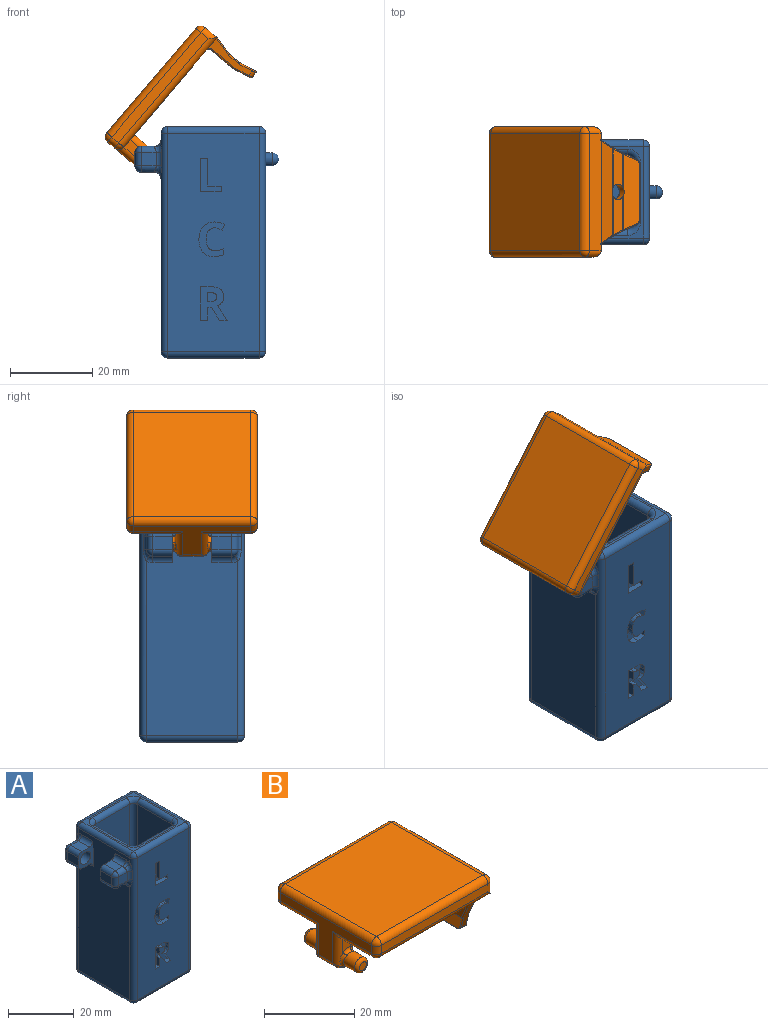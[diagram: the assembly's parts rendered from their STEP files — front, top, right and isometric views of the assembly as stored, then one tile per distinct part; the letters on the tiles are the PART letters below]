
ASSEMBLY  parts=2 mates=1
PART A: 139 faces, bbox 34.9x25.4x56.2 mm
  f0: plane 53.02x22.23mm, normal (-1,0,0), area 1058.3mm2, adj f78,f79,f88,f89,f97,f102,f119,f120
  f1: plane 22.23x22.23mm, normal (0,0,1), area 63.5mm2, adj f60,f65,f66,f69,f70,f72,f73,f74
  f2: plane 53.02x22.23mm, normal (0,-1,0), area 1099mm2, adj f17,f18,f19,f20,f21,f22,f23,f24
  f3: plane 53.02x22.23mm, normal (1,0,0), area 1170.5mm2, adj f81,f82,f90,f91,f137
  f4: plane 53.02x22.23mm, normal (0,1,0), area 1178.4mm2, adj f80,f89,f90,f94
  f5: plane 22.23x22.23mm, normal (0,0,-1), area 494mm2, adj f75,f79,f80,f81
  f6: plane 49.21x14.61mm, normal (1,0,0), area 718.7mm2, adj f58,f59,f68,f69
  f7: plane 49.21x14.61mm, normal (0,-1,0), area 718.7mm2, adj f63,f68,f71,f74
  f8: plane 49.21x14.61mm, normal (-1,0,0), area 718.7mm2, adj f61,f62,f70,f71
  f9: plane 49.21x14.61mm, normal (0,1,0), area 718.7mm2, adj f55,f59,f60,f61
  f10: plane 14.61x14.61mm, normal (0,0,1), area 213.3mm2, adj f55,f58,f62,f63
  f11: plane 2.21x1.59mm, normal (-1,0,0), area 3.5mm2, adj f12,f29,f30,f54
  f12: plane 1.59x0.53mm, normal (0,0,1), area 0.8mm2, adj f11,f13,f30,f54
  f13: extruded ~1.59x1.24mm, area 2mm2, adj f12,f14,f30,f54
  f14: extruded ~1.59x0.83mm, area 1.5mm2, adj f13,f15,f30,f54
  f15: extruded ~1.59x0.86mm, area 1.6mm2, adj f14,f16,f30,f54
  f16: extruded ~1.59x1.22mm, area 2mm2, adj f15,f29,f30,f54
  f17: plane 1.59x0.92mm, normal (0,0,1), area 1.5mm2, adj f2,f18,f28,f30
  f18: plane 3.14x1.95mm, normal (0.85,0,0.53), area 5.9mm2, adj f2,f17,f19,f30
  f19: plane 1.93x1.59mm, normal (0,0,1), area 3.1mm2, adj f2,f18,f20,f30
  f20: plane 3.57x2.41mm, normal (-0.83,0,-0.56), area 6.8mm2, adj f2,f19,f21,f30
  f21: extruded ~1.59x1.13mm, area 2.3mm2, adj f2,f20,f22,f30
  f22: extruded ~1.59x1.28mm, area 2.2mm2, adj f2,f21,f23,f30
  f23: extruded ~1.85x1.59mm, area 3.3mm2, adj f2,f22,f24,f30
  f24: extruded ~2.47x1.59mm, area 4.1mm2, adj f2,f23,f25,f30
  f25: plane 2.38x1.59mm, normal (0,0,-1), area 3.8mm2, adj f2,f24,f26,f30
  f26: plane 8.19x1.59mm, normal (1,0,0), area 13mm2, adj f2,f25,f27,f30
  f27: plane 1.74x1.59mm, normal (0,0,1), area 2.8mm2, adj f2,f26,f28,f30
  f28: plane 3.14x1.59mm, normal (-1,0,0), area 5mm2, adj f2,f17,f27,f30
  f29: plane 1.59x0.56mm, normal (0,0,-1), area 0.9mm2, adj f11,f16,f30,f54
  f30: plane 8.19x6.54mm, normal (0,-1,0), area 32.7mm2, adj f11,f12,f13,f14,f15,f16,f17,f18
  f31: extruded ~1.59x0.91mm, area 1.5mm2, adj f2,f32,f45,f46
  f32: extruded ~1.59x0.92mm, area 1.6mm2, adj f2,f31,f33,f46
  f33: plane 1.59x1.41mm, normal (-0.93,0,0.37), area 2.4mm2, adj f2,f32,f34,f46
  f34: extruded ~2.4x1.59mm, area 3.9mm2, adj f2,f33,f35,f46
  f35: extruded ~2.04x1.59mm, area 3.4mm2, adj f2,f34,f36,f46
  f36: extruded ~1.59x1.47mm, area 3.2mm2, adj f2,f35,f37,f46
  f37: extruded ~2.24x1.59mm, area 3.7mm2, adj f2,f36,f38,f46
  f38: extruded ~3.11x1.59mm, area 5.3mm2, adj f2,f37,f39,f46
  f39: extruded ~2.73x1.59mm, area 4.8mm2, adj f2,f38,f40,f46
  f40: extruded ~2.25x1.59mm, area 3.7mm2, adj f2,f39,f41,f46
  f41: plane 1.59x1.45mm, normal (-1,0,0), area 2.3mm2, adj f2,f40,f42,f46
  f42: extruded ~2.09x1.59mm, area 3.4mm2, adj f2,f41,f43,f46
  f43: extruded ~2.74x2.05mm, area 6.2mm2, adj f2,f42,f44,f46
  f44: extruded ~2.05x1.59mm, area 3.4mm2, adj f2,f43,f45,f46
  f45: extruded ~1.59x1.52mm, area 2.8mm2, adj f2,f31,f44,f46
  f46: plane 8.41x6.24mm, normal (0,-1,0), area 23.5mm2, adj f31,f32,f33,f34,f35,f36,f37,f38
  f47: plane 5.06x1.59mm, normal (0,0,1), area 8mm2, adj f2,f48,f52,f53
  f48: plane 1.59x1.43mm, normal (-1,0,0), area 2.3mm2, adj f2,f47,f49,f53
  f49: plane 3.32x1.59mm, normal (0,0,-1), area 5.3mm2, adj f2,f48,f50,f53
  f50: plane 6.75x1.59mm, normal (-1,0,0), area 10.7mm2, adj f2,f49,f51,f53
  f51: plane 1.74x1.59mm, normal (0,0,-1), area 2.8mm2, adj f2,f50,f52,f53
  f52: plane 8.19x1.59mm, normal (1,0,0), area 13mm2, adj f2,f47,f51,f53
  f53: plane 8.19x5.06mm, normal (0,-1,0), area 19mm2, adj f47,f48,f49,f50,f51,f52
  f54: plane 2.21x2.17mm, normal (0,-1,0), area 4.2mm2, adj f11,f12,f13,f14,f15,f16,f29
  f55: cylinder r=1.59mm len=14.61mm, axis (-1,0,0), area 36.4mm2, adj f9,f10,f56,f57
  f56: sphere r=1.59mm, area 4mm2, adj f55,f58,f59
  f57: sphere r=1.59mm, area 4mm2, adj f55,f61,f62
  f58: cylinder r=1.59mm len=14.61mm, axis (0,1,0), area 36.4mm2, adj f6,f10,f56,f64
  f59: cylinder r=1.59mm len=49.21mm, axis (0,0,-1), area 122.7mm2, adj f6,f9,f56,f65
  f60: cylinder r=1.59mm len=14.61mm, axis (1,0,0), area 36.4mm2, adj f1,f9,f65,f66
  f61: cylinder r=1.59mm len=49.21mm, axis (0,0,1), area 122.7mm2, adj f8,f9,f57,f66
  f62: cylinder r=1.59mm len=14.61mm, axis (0,-1,0), area 36.4mm2, adj f8,f10,f57,f67
  f63: cylinder r=1.59mm len=14.61mm, axis (1,0,0), area 36.4mm2, adj f7,f10,f64,f67
  f64: sphere r=1.59mm, area 4mm2, adj f58,f63,f68
  f65: torus R=3.17mm, axis (0,0,1), area 8.5mm2, adj f1,f59,f60,f69
  f66: torus R=3.17mm, axis (0,0,1), area 8.5mm2, adj f1,f60,f61,f70
  f67: sphere r=1.59mm, area 4mm2, adj f62,f63,f71
  f68: cylinder r=1.59mm len=49.21mm, axis (0,0,1), area 122.7mm2, adj f6,f7,f64,f72
  f69: cylinder r=1.59mm len=14.61mm, axis (0,-1,0), area 36.4mm2, adj f1,f6,f65,f72
  f70: cylinder r=1.59mm len=14.61mm, axis (0,1,0), area 36.4mm2, adj f1,f8,f66,f73
  f71: cylinder r=1.59mm len=49.21mm, axis (0,0,-1), area 122.7mm2, adj f7,f8,f67,f73
  f72: torus R=3.17mm, axis (0,0,1), area 8.5mm2, adj f1,f68,f69,f74
  f73: torus R=3.17mm, axis (0,0,1), area 8.5mm2, adj f1,f70,f71,f74
  f74: cylinder r=1.59mm len=14.61mm, axis (-1,0,0), area 36.4mm2, adj f1,f7,f72,f73
  f75: cylinder r=1.59mm len=22.23mm, axis (1,0,0), area 55.4mm2, adj f2,f5,f76,f77
  f76: sphere r=1.59mm, area 4mm2, adj f75,f78,f79
  f77: sphere r=1.59mm, area 4mm2, adj f75,f81,f82
  f78: cylinder r=1.59mm len=53.02mm, axis (0,0,1), area 126.4mm2, adj f0,f2,f76,f84,f128,f129,f130
  f79: cylinder r=1.59mm len=22.23mm, axis (0,-1,0), area 55.4mm2, adj f0,f5,f76,f85
  f80: cylinder r=1.59mm len=22.23mm, axis (-1,0,0), area 55.4mm2, adj f4,f5,f85,f86
  f81: cylinder r=1.59mm len=22.23mm, axis (0,1,0), area 55.4mm2, adj f3,f5,f77,f86
  f82: cylinder r=1.59mm len=53.02mm, axis (0,0,-1), area 132.2mm2, adj f2,f3,f77,f87
  f83: cylinder r=1.59mm len=22.23mm, axis (-1,0,0), area 55.4mm2, adj f1,f2,f84,f87
  f84: sphere r=1.59mm, area 4mm2, adj f78,f83,f88
  f85: sphere r=1.59mm, area 4mm2, adj f79,f80,f89
  f86: sphere r=1.59mm, area 4mm2, adj f80,f81,f90
  f87: sphere r=1.59mm, area 4mm2, adj f82,f83,f91
  f88: cylinder r=1.59mm len=22.23mm, axis (0,1,0), area 55.4mm2, adj f0,f1,f84,f92
  f89: cylinder r=1.59mm len=53.02mm, axis (0,0,-1), area 126.4mm2, adj f0,f4,f85,f92,f121,f122,f123
  f90: cylinder r=1.59mm len=53.02mm, axis (0,0,1), area 132.2mm2, adj f3,f4,f86,f93
  f91: cylinder r=1.59mm len=22.23mm, axis (0,-1,0), area 55.4mm2, adj f1,f3,f87,f93
  f92: sphere r=1.59mm, area 4mm2, adj f88,f89,f94
  f93: sphere r=1.59mm, area 4mm2, adj f90,f91,f94
  f94: cylinder r=1.59mm len=22.23mm, axis (1,0,0), area 55.4mm2, adj f1,f4,f92,f93
  f95: plane 3.6x3.18mm, normal (0,1,0), area 11.4mm2, adj f113,f116,f118,f122
  f96: plane 4.76x3.18mm, normal (0,0,-1), area 15.1mm2, adj f97,f112,f113,f125
  f97: plane 9.53x6.35mm, normal (0,-1,0), area 24.8mm2, adj f0,f96,f98,f99,f112,f115,f119,f125
  f98: plane 4.76x3.18mm, normal (0,0,1), area 15.1mm2, adj f97,f115,f118,f119
  f99: plane 4.76x3.18mm, normal (-1,0,0), area 15.1mm2, adj f97,f112,f115,f116
  f100: plane 3.6x3.18mm, normal (0,-1,0), area 11.4mm2, adj f105,f108,f111,f129
  f101: plane 4.76x3.18mm, normal (0,0,1), area 15.1mm2, adj f102,f109,f111,f126
  f102: plane 9.53x6.35mm, normal (0,1,0), area 24.8mm2, adj f0,f101,f103,f104,f106,f109,f126,f132
  f103: plane 4.76x3.18mm, normal (0,0,-1), area 15.1mm2, adj f102,f105,f106,f132
  f104: plane 4.76x3.18mm, normal (-1,0,0), area 15.1mm2, adj f102,f106,f108,f109
  f105: cylinder r=1.59mm len=3.6mm, axis (-1,0,0), area 8.3mm2, adj f100,f103,f107,f130,f131
  f106: cylinder r=1.59mm len=4.76mm, axis (0,1,0), area 11.9mm2, adj f102,f103,f104,f107
  f107: sphere r=1.59mm, area 4mm2, adj f105,f106,f108
  f108: cylinder r=1.59mm len=3.18mm, axis (0,0,-1), area 7.9mm2, adj f100,f104,f107,f110
  f109: cylinder r=1.59mm len=4.76mm, axis (0,-1,0), area 11.9mm2, adj f101,f102,f104,f110
  f110: sphere r=1.59mm, area 4mm2, adj f108,f109,f111
  f111: cylinder r=1.59mm len=3.6mm, axis (1,0,0), area 8.3mm2, adj f100,f101,f110,f127,f128
  f112: cylinder r=1.59mm len=4.76mm, axis (0,1,0), area 11.9mm2, adj f96,f97,f99,f114
  f113: cylinder r=1.59mm len=3.6mm, axis (1,0,0), area 8.3mm2, adj f95,f96,f114,f123,f124
  f114: sphere r=1.59mm, area 4mm2, adj f112,f113,f116
  f115: cylinder r=1.59mm len=4.76mm, axis (0,-1,0), area 11.9mm2, adj f97,f98,f99,f117
  f116: cylinder r=1.59mm len=3.18mm, axis (0,0,1), area 7.9mm2, adj f95,f99,f114,f117
  f117: sphere r=1.59mm, area 4mm2, adj f115,f116,f118
  f118: cylinder r=1.59mm len=3.6mm, axis (-1,0,0), area 8.3mm2, adj f95,f98,f117,f120,f121
  f119: cylinder r=1.59mm len=4.76mm, axis (0,1,0), area 11.9mm2, adj f0,f97,f98,f120
  f120: torus R=3.17mm, axis (-1,0,0), area 2.8mm2, adj f0,f118,f119,f121
  f121: bspline ~3.35x1.8mm, area 4.1mm2, adj f89,f118,f120,f122
  f122: cylinder r=1.59mm len=3.18mm, axis (0,0,-1), area 5.3mm2, adj f89,f95,f121,f123
  f123: bspline ~3.49x1.8mm, area 4.1mm2, adj f89,f113,f122,f124
  f124: torus R=3.17mm, axis (-1,0,0), area 2.8mm2, adj f0,f113,f123,f125
  f125: cylinder r=1.59mm len=4.76mm, axis (0,-1,0), area 11.9mm2, adj f0,f96,f97,f124
  f126: cylinder r=1.59mm len=4.76mm, axis (0,1,0), area 11.9mm2, adj f0,f101,f102,f127
  f127: torus R=3.17mm, axis (-1,0,0), area 2.8mm2, adj f0,f111,f126,f128
  f128: bspline ~3.35x1.8mm, area 4.1mm2, adj f78,f111,f127,f129
  f129: cylinder r=1.59mm len=3.18mm, axis (0,0,1), area 5.3mm2, adj f78,f100,f128,f130
  f130: bspline ~3.49x1.8mm, area 4.1mm2, adj f78,f105,f129,f131
  f131: torus R=3.17mm, axis (-1,0,0), area 2.8mm2, adj f0,f105,f130,f132
  f132: cylinder r=1.59mm len=4.76mm, axis (0,-1,0), area 11.9mm2, adj f0,f102,f103,f131
  f133: cylinder r=2.22mm len=4.45mm, axis (0,1,0), area 62.1mm2, adj f102,f134
  f134: plane 4.45x4.45mm, normal (0,1,0), area 15.5mm2, adj f133
  f135: cylinder r=2.22mm len=4.45mm, axis (0,-1,0), area 62.1mm2, adj f97,f136
  f136: plane 4.45x4.45mm, normal (0,-1,0), area 15.5mm2, adj f135
  f137: cylinder r=1.59mm len=3.18mm, axis (-1,0,0), area 15.8mm2, adj f3,f138
  f138: sphere r=1.59mm, area 15.8mm2, adj f137
PART B: 127 faces, bbox 36.6x31.8x18.2 mm
  f0: plane 26.99x8.51mm, normal (1,0,0), area 52.3mm2, adj f14,f15,f17,f47,f48,f87,f88,f89
  f1: plane 4.13x2.38mm, normal (0,-1,0), area 8.9mm2, adj f12,f87,f90,f99
  f2: plane 18.28x4.34mm, normal (0.97,0,0.23), area 73mm2, adj f25,f59,f62,f65,f67,f70,f71,f74
  f3: plane 18.4x4.48mm, normal (-0.97,0,-0.23), area 74.6mm2, adj f51,f52,f53,f73,f76,f78,f81,f83
  f4: plane 35x10.69mm, normal (0,0,-1), area 60.1mm2, adj f14,f19,f24,f27,f28,f32,f47,f49
  f5: plane 13.09x1.41mm, normal (0,0,-1), area 18.5mm2, adj f52,f65,f72,f75
  f6: plane 23.97x6.97mm, normal (-1,0,0), area 133.5mm2, adj f46,f50,f54,f78,f80,f83
  f7: plane 9.33x3.1mm, normal (1,0,0), area 25.3mm2, adj f25,f56,f59,f60
  f8: plane 9.33x3.1mm, normal (1,0,0), area 25.3mm2, adj f25,f64,f68,f70
  f9: plane 24.77x4.73mm, normal (0.97,0,-0.23), area 110.7mm2, adj f24,f25,f56,f57,f63,f64
  f10: plane 33.34x2.22mm, normal (0,1,0), area 74.1mm2, adj f29,f32,f34,f35
  f11: plane 33.34x2.22mm, normal (0,-1,0), area 74.1mm2, adj f39,f40,f44,f45
  f12: plane 35x10.69mm, normal (0,0,-1), area 60.1mm2, adj f1,f15,f24,f26,f38,f44,f48,f55
  f13: plane 33.34x28.58mm, normal (0,0,1), area 952.6mm2, adj f33,f34,f40,f41
  f14: plane 28.04x1.59mm, normal (0,-1,0), area 43mm2, adj f0,f4,f16,f17,f47,f85
  f15: plane 28.04x1.59mm, normal (0,1,0), area 43mm2, adj f0,f12,f16,f17,f48,f85
  f16: plane 26.99x1.35mm, normal (-1,0,0), area 36.4mm2, adj f14,f15,f17,f85
  f17: plane 26.99x26.99mm, normal (0,0,-1), area 728.3mm2, adj f0,f14,f15,f16
  f18: plane 28.58x10.73mm, normal (-1,0,0), area 101.3mm2, adj f28,f29,f33,f38,f39,f90,f91,f92
  f19: plane 4.13x2.38mm, normal (0,1,0), area 8.9mm2, adj f4,f88,f91,f96
  f20: cylinder r=1.91mm len=4.02mm, axis (0,1,0), area 39.6mm2, adj f99,f100,f101,f102,f103,f104,f106
  f21: plane 2.16x2.16mm, normal (0,-1,0), area 3.7mm2, adj f106
  f22: cylinder r=1.91mm len=4.02mm, axis (0,-1,0), area 39.6mm2, adj f93,f94,f95,f96,f97,f98,f105
  f23: plane 2.16x2.16mm, normal (0,1,0), area 3.7mm2, adj f105
  f24: plane 28.58x3.81mm, normal (1,0,0), area 108.9mm2, adj f4,f9,f12,f35,f41,f45
  f25: cylinder r=1.91mm len=3.81mm, axis (1,0,0), area 20.8mm2, adj f2,f7,f8,f9,f56,f59,f64,f70
  f26: plane 11.74x4.72mm, normal (0,-0.93,-0.37), area 21.1mm2, adj f12,f53,f54,f55,f63,f66,f67,f68
  f27: plane 11.74x4.72mm, normal (0,0.93,-0.37), area 21.1mm2, adj f4,f49,f50,f51,f57,f58,f60,f61
  f28: cylinder r=1.59mm len=12.07mm, axis (0,1,0), area 28.1mm2, adj f4,f18,f30,f91
  f29: cylinder r=1.59mm len=2.22mm, axis (0,0,-1), area 5.5mm2, adj f10,f18,f30,f31
  f30: sphere r=1.59mm, area 5.4mm2, adj f28,f29,f32
  f31: sphere r=1.59mm, area 5.4mm2, adj f29,f33,f34
  f32: cylinder r=1.59mm len=34.93mm, axis (1,0,0), area 85.1mm2, adj f4,f10,f30,f35
  f33: cylinder r=1.59mm len=28.58mm, axis (0,1,0), area 71.3mm2, adj f13,f18,f31,f36
  f34: cylinder r=1.59mm len=33.34mm, axis (1,0,0), area 83.1mm2, adj f10,f13,f31,f37
  f35: cylinder r=1.59mm len=3.81mm, axis (0,0,-1), area 7.5mm2, adj f10,f24,f32,f37
  f36: sphere r=1.59mm, area 4mm2, adj f33,f39,f40
  f37: sphere r=1.59mm, area 2.5mm2, adj f34,f35,f41
  f38: cylinder r=1.59mm len=12.07mm, axis (0,1,0), area 28.1mm2, adj f12,f18,f42,f90
  f39: cylinder r=1.59mm len=2.22mm, axis (0,0,1), area 5.5mm2, adj f11,f18,f36,f42
  f40: cylinder r=1.59mm len=33.34mm, axis (-1,0,0), area 83.1mm2, adj f11,f13,f36,f43
  f41: cylinder r=1.59mm len=28.58mm, axis (0,1,0), area 71.3mm2, adj f13,f24,f37,f43
  f42: sphere r=1.59mm, area 4mm2, adj f38,f39,f44
  f43: sphere r=1.59mm, area 4mm2, adj f40,f41,f45
  f44: cylinder r=1.59mm len=34.93mm, axis (-1,0,0), area 85.1mm2, adj f11,f12,f42,f45
  f45: cylinder r=1.59mm len=3.81mm, axis (0,0,1), area 7.5mm2, adj f11,f24,f43,f44
  f46: cylinder r=0.95mm len=24.91mm, axis (0,-1,0), area 27.5mm2, adj f6,f49,f55,f85
  f47: cylinder r=0.95mm len=11.27mm, axis (0,1,0), area 15.7mm2, adj f0,f4,f14,f88
  f48: cylinder r=0.95mm len=11.27mm, axis (0,1,0), area 15.7mm2, adj f0,f12,f15,f87
  f49: bspline ~1.48x1.18mm, area 0.6mm2, adj f4,f27,f46,f50,f85
  f50: cylinder r=0.32mm len=7.09mm, axis (0,-0.37,-0.93), area 3.7mm2, adj f6,f27,f49,f84
  f51: cylinder r=0.32mm len=3.74mm, axis (0.21,-0.36,-0.91), area 1.9mm2, adj f3,f27,f73,f84
  f52: cylinder r=0.32mm len=13.09mm, axis (0,-1,0), area 5.6mm2, adj f3,f5,f73,f76
  f53: cylinder r=0.32mm len=3.74mm, axis (-0.21,-0.36,0.91), area 1.9mm2, adj f3,f26,f76,f77
  f54: cylinder r=0.32mm len=7.09mm, axis (0,-0.37,0.93), area 3.7mm2, adj f6,f26,f55,f77
  f55: bspline ~1.48x1.18mm, area 0.6mm2, adj f12,f26,f46,f54,f85
  f56: cylinder r=0.32mm len=9.5mm, axis (0,-1,0), area 0.7mm2, adj f7,f9,f25,f58
  f57: cylinder r=0.32mm len=4.83mm, axis (0.21,0.36,0.91), area 2.5mm2, adj f4,f9,f27,f58
  f58: bspline ~0.48x0.45mm, area 0.1mm2, adj f27,f56,f57,f60
  f59: cylinder r=0.32mm len=8.2mm, axis (0,1,0), area 0.6mm2, adj f2,f7,f25,f61
  f60: cylinder r=0.32mm len=3.22mm, axis (0,0.37,0.93), area 1.7mm2, adj f7,f27,f58,f61
  f61: bspline ~0.45x0.44mm, area 0.1mm2, adj f27,f59,f60,f62
  f62: cylinder r=0.32mm len=3.73mm, axis (-0.21,0.36,0.91), area 2mm2, adj f2,f27,f61,f71
  f63: cylinder r=0.32mm len=4.83mm, axis (-0.21,0.36,-0.91), area 2.5mm2, adj f9,f12,f26,f66
  f64: cylinder r=0.32mm len=9.5mm, axis (0,-1,0), area 0.7mm2, adj f8,f9,f25,f66
  f65: cylinder r=0.32mm len=13.09mm, axis (0,-1,0), area 7.5mm2, adj f2,f5,f71,f74
  f66: bspline ~0.45x0.38mm, area 0.1mm2, adj f26,f63,f64,f68
  f67: cylinder r=0.32mm len=3.73mm, axis (0.21,0.36,-0.91), area 2mm2, adj f2,f26,f69,f74
  f68: cylinder r=0.32mm len=3.22mm, axis (0,0.37,-0.93), area 1.7mm2, adj f8,f26,f66,f69
  f69: bspline ~0.45x0.44mm, area 0.1mm2, adj f26,f67,f68,f70
  f70: cylinder r=0.32mm len=8.2mm, axis (0,1,0), area 0.6mm2, adj f2,f8,f25,f69
  f71: bspline ~1.57x1.38mm, area 1mm2, adj f2,f62,f65,f72
  f72: cylinder r=1.59mm len=1.6mm, axis (1,0,0), area 2.7mm2, adj f5,f27,f71,f73
  f73: bspline ~1.47x1.04mm, area 0.8mm2, adj f3,f51,f52,f72
  f74: bspline ~1.57x1.38mm, area 1mm2, adj f2,f65,f67,f75
  f75: cylinder r=1.59mm len=1.6mm, axis (1,0,0), area 2.7mm2, adj f5,f26,f74,f76
  f76: bspline ~1.47x1.04mm, area 0.8mm2, adj f3,f52,f53,f75
  f77: sphere r=0.32mm, area 0mm2, adj f53,f54,f78
  f78: cylinder r=0.32mm len=7.61mm, axis (0,1,0), area 0.6mm2, adj f3,f6,f77,f79
  f79: sphere r=0.32mm, area 0mm2, adj f78,f80,f81
  f80: torus R=2.22mm, axis (1,0,0), area 4.7mm2, adj f6,f25,f79,f82
  f81: bspline ~3.18x0.97mm, area 1.8mm2, adj f3,f25,f79,f82
  f82: sphere r=0.32mm, area 0mm2, adj f80,f81,f83
  f83: cylinder r=0.32mm len=7.61mm, axis (0,1,0), area 0.6mm2, adj f3,f6,f82,f84
  f84: sphere r=0.32mm, area 0mm2, adj f50,f51,f83
  f85: cylinder r=0.32mm len=26.99mm, axis (0,-1,0), area 10mm2, adj f4,f12,f14,f15,f16,f46,f49,f55
  f86: plane 7.05x2.38mm, normal (0,0,-1), area 16.2mm2, adj f89,f92,f109,f110,f111,f116,f120,f122
  f87: cylinder r=1.59mm len=8.41mm, axis (0,0,1), area 14.9mm2, adj f0,f1,f12,f48,f101,f107
  f88: cylinder r=1.59mm len=8.41mm, axis (0,0,-1), area 14.9mm2, adj f0,f4,f19,f47,f98,f126
  f89: cylinder r=1.59mm len=6.63mm, axis (0,1,0), area 13.8mm2, adj f0,f86,f107,f108,f125,f126
  f90: cylinder r=1.59mm len=9.23mm, axis (0,0,1), area 18.2mm2, adj f1,f18,f38,f100,f112
  f91: cylinder r=1.59mm len=9.23mm, axis (0,0,-1), area 18.2mm2, adj f18,f19,f28,f94,f117
  f92: cylinder r=1.59mm len=6.09mm, axis (0,1,0), area 13.3mm2, adj f18,f86,f112,f115,f117,f118
  f93: bspline ~0.91x0.83mm, area 0mm2, adj f22,f94,f95,f119
  f94: bspline ~4.79x1.5mm, area 3.9mm2, adj f22,f91,f93,f96,f118,f120
  f95: bspline ~2.72x0.87mm, area 1mm2, adj f22,f93,f97,f119,f122
  f96: torus R=2.73mm, axis (0,-1,0), area 2.6mm2, adj f19,f22,f94,f98
  f97: bspline ~1.24x0.96mm, area 0.5mm2, adj f22,f95,f98,f123
  f98: bspline ~4.86x1.74mm, area 3.6mm2, adj f22,f88,f96,f97,f124,f125
  f99: torus R=2.73mm, axis (0,-1,0), area 2.6mm2, adj f1,f20,f100,f101
  f100: bspline ~4.79x1.5mm, area 3.9mm2, adj f20,f90,f99,f102,f115,f116
  f101: bspline ~4.86x1.74mm, area 3.6mm2, adj f20,f87,f99,f103,f108,f109
  f102: bspline ~0.84x0.74mm, area 0mm2, adj f20,f100,f104,f113
  f103: bspline ~1.28x0.95mm, area 0.4mm2, adj f20,f101,f104,f110
  f104: bspline ~2.94x0.87mm, area 1mm2, adj f20,f102,f103,f111,f113
  f105: torus R=1.08mm, axis (0,1,0), area 13.1mm2, adj f22,f23
  f106: torus R=1.08mm, axis (0,-1,0), area 13.1mm2, adj f20,f21
  f107: bspline ~1.26x1.26mm, area 0.4mm2, adj f87,f89,f108
  f108: bspline ~1.71x1.29mm, area 1mm2, adj f89,f101,f107,f109
  f109: bspline ~0.93x0.87mm, area 0.1mm2, adj f86,f101,f108,f110
  f110: bspline ~0.78x0.66mm, area 0.3mm2, adj f86,f103,f109,f111
  f111: bspline ~2.22x0.64mm, area 1mm2, adj f86,f104,f110,f114
  f112: bspline ~1.53x1.53mm, area 0.9mm2, adj f90,f92,f115
  f113: bspline ~0.04x0.04mm, area 0mm2, adj f102,f104,f114,f116
  f114: bspline ~0.63x0.37mm, area 0mm2, adj f111,f113,f116
  f115: bspline ~0.96x0.93mm, area 0.5mm2, adj f92,f100,f112,f116
  f116: bspline ~1.4x1.17mm, area 0.7mm2, adj f86,f100,f113,f114,f115
  f117: bspline ~1.53x1.53mm, area 0.9mm2, adj f91,f92,f118
  f118: bspline ~0.96x0.93mm, area 0.5mm2, adj f92,f94,f117,f120
  f119: bspline ~0.04x0.04mm, area 0mm2, adj f93,f95,f120,f121
  f120: bspline ~1.4x1.17mm, area 0.7mm2, adj f86,f94,f118,f119,f121
  f121: bspline ~0.63x0.37mm, area 0mm2, adj f119,f120,f122
  f122: bspline ~2.18x0.64mm, area 1mm2, adj f86,f95,f121,f123
  f123: bspline ~0.78x0.67mm, area 0.3mm2, adj f86,f97,f122,f124
  f124: bspline ~0.93x0.87mm, area 0.1mm2, adj f86,f98,f123,f125
  f125: bspline ~1.71x1.29mm, area 1mm2, adj f89,f98,f124,f126
  f126: bspline ~1.26x1.26mm, area 0.4mm2, adj f88,f89,f125
PLACE A t=(-58.99,-8.12,-16.15)mm fixed
PLACE B rot(axis=(0,-1,0),49.6deg) t=(-68.21,-11.25,37.25)mm
MATE cylindrical B.f20 <-> A.f135  axis (0,1,0) through (-62.17,0.99,32.11)mm
